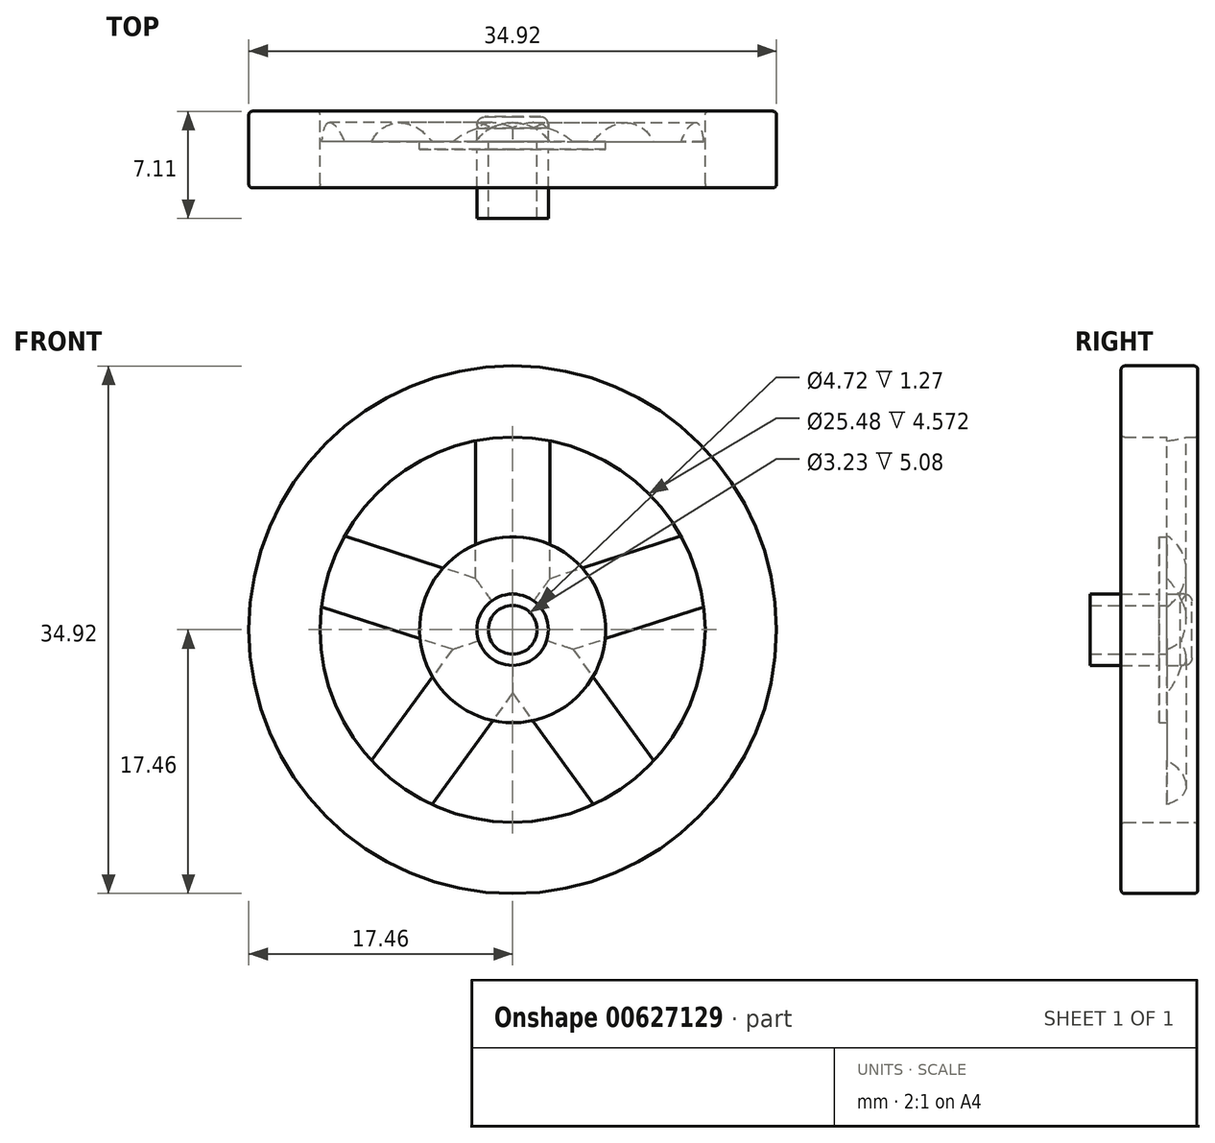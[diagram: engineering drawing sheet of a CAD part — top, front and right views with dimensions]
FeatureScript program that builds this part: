
annotation { "Feature Type Name" : "Feature", "Feature Type Description" : "" }
export const myFeature = defineFeature(function(context is Context, id is Id, definition is map)
    precondition{}
    {
        {
            var Q0;
            Q0=qCreatedBy(makeId("Front.planeOp"),FACE);
            var sketch = newSketch(context, id + "F0", { "sketchPlane" : qUnion([Q0])});
            skCircle(sketch, "E0", {"center": v(0, 0) * mm, "radius": 17.46 * mm});
            skCircle(sketch, "E1", {"center": v(0, 0) * mm, "radius": 6.16 * mm});
            skCircle(sketch, "E2", {"center": v(0, 0) * mm, "radius": 2.36 * mm});
            skLineSegment(sketch, "E3.trimOffspring", {"start": v(-2.46, 3.4) * mm, "end": v(-2.46, 12.5) * mm});
            skLineSegment(sketch, "E4.trimOffspring", {"start": v(2.46, 3.4) * mm, "end": v(2.46, 12.5) * mm});
            skCircle(sketch, "E5.0", {"center": v(0, 0) * mm, "radius": 12.74 * mm});
            skLineSegment(sketch, "E6.1.0", {"start": v(-3.99, -1.3) * mm, "end": v(-12.65, 1.52) * mm});
            skLineSegment(sketch, "E6.1.1", {"start": v(-2.46, 3.4) * mm, "end": v(-11.12, 6.2) * mm});
            skLineSegment(sketch, "E6.2.0", {"start": v(0, -4.2) * mm, "end": v(-5.35, -11.56) * mm});
            skLineSegment(sketch, "E6.2.1", {"start": v(-3.99, -1.3) * mm, "end": v(-9.34, -8.66) * mm});
            skLineSegment(sketch, "E6.3.0", {"start": v(3.99, -1.3) * mm, "end": v(9.34, -8.66) * mm});
            skLineSegment(sketch, "E6.3.1", {"start": v(0, -4.2) * mm, "end": v(5.35, -11.56) * mm});
            skLineSegment(sketch, "E6.4.0", {"start": v(2.46, 3.4) * mm, "end": v(11.12, 6.2) * mm});
            skLineSegment(sketch, "E6.4.1", {"start": v(3.99, -1.3) * mm, "end": v(12.65, 1.52) * mm});
            skSolve(sketch);
        }
        {
            var Q0;
            Q0=makeQuery(id+"F0.imprint","IMPRINT",FACE,{"disambiguationData":[TD([[makeQuery(id+"F0.imprint","IMPRINT",EDGE,{"derivedFrom":sQuery(id+"F0.wireOp",EDGE,"E2")}),-1.0]])]});
            var Q1;
            {var subQ0=sQuery(id+"F0.wireOp",EDGE,"E5.0");var subQ1=sQuery(id+"F0.wireOp",EDGE,"E3.trimOffspring");var subQ2=makeQuery(id+"F0.imprint","INTERSECT",VERTEX,{"derivedFrom":[subQ1,subQ0]});Q1=makeQuery(id+"F0.imprint","IMPRINT",FACE,{"disambiguationData":[TD([[makeQuery(id+"F0.imprint","IMPRINT",EDGE,{"disambiguationData":[TD([[subQ2,1.0]])],"derivedFrom":subQ1}),-1.0]])]});}
            var Q2;
            {var subQ0=sQuery(id+"F0.wireOp",EDGE,"E6.3.0");var subQ1=sQuery(id+"F0.wireOp",EDGE,"E5.0");var subQ2=makeQuery(id+"F0.imprint","INTERSECT",VERTEX,{"derivedFrom":[subQ1,subQ0]});Q2=makeQuery(id+"F0.imprint","IMPRINT",FACE,{"disambiguationData":[TD([[makeQuery(id+"F0.imprint","IMPRINT",EDGE,{"disambiguationData":[TD([[subQ2,1.0]])],"derivedFrom":subQ1}),1.0]])]});}
            var Q3;
            {var subQ0=sQuery(id+"F0.wireOp",EDGE,"E6.2.0");var subQ1=sQuery(id+"F0.wireOp",EDGE,"E5.0");var subQ2=makeQuery(id+"F0.imprint","INTERSECT",VERTEX,{"derivedFrom":[subQ1,subQ0]});Q3=makeQuery(id+"F0.imprint","IMPRINT",FACE,{"disambiguationData":[TD([[makeQuery(id+"F0.imprint","IMPRINT",EDGE,{"disambiguationData":[TD([[subQ2,1.0]])],"derivedFrom":subQ1}),1.0]])]});}
            var Q4;
            {var subQ0=sQuery(id+"F0.wireOp",EDGE,"E6.1.0");var subQ1=sQuery(id+"F0.wireOp",EDGE,"E5.0");var subQ2=makeQuery(id+"F0.imprint","INTERSECT",VERTEX,{"derivedFrom":[subQ1,subQ0]});Q4=makeQuery(id+"F0.imprint","IMPRINT",FACE,{"disambiguationData":[TD([[makeQuery(id+"F0.imprint","IMPRINT",EDGE,{"disambiguationData":[TD([[subQ2,1.0]])],"derivedFrom":subQ1}),1.0]])]});}
            var Q5;
            {var subQ0=sQuery(id+"F0.wireOp",EDGE,"E6.4.0");var subQ1=sQuery(id+"F0.wireOp",EDGE,"E5.0");var subQ2=makeQuery(id+"F0.imprint","INTERSECT",VERTEX,{"derivedFrom":[subQ1,subQ0]});Q5=makeQuery(id+"F0.imprint","IMPRINT",FACE,{"disambiguationData":[TD([[makeQuery(id+"F0.imprint","IMPRINT",EDGE,{"disambiguationData":[TD([[subQ2,1.0]])],"derivedFrom":subQ1}),1.0]])]});}
            extrude(context, id + "F1", {"entities" : qUnion([Q0, Q1, Q2, Q3, Q4, Q5]), "depth" : 1.27 * mm, "offsetDistance" : 25.4 * mm});
        }
        {
            var Q0;
            Q0=makeQuery(id+"F1.opExtrude","CAP_EDGE",EDGE,{"disambiguationData":[OSD([sQuery(id+"F0.wireOp",EDGE,"E6.2.0")])],"isStart":true});
            var Q1;
            Q1=makeQuery(id+"F1.opExtrude","CAP_EDGE",EDGE,{"disambiguationData":[OSD([sQuery(id+"F0.wireOp",EDGE,"E6.2.1")])],"isStart":true});
            var Q2;
            Q2=makeQuery(id+"F1.opExtrude","CAP_EDGE",EDGE,{"disambiguationData":[OSD([sQuery(id+"F0.wireOp",EDGE,"E6.1.0")])],"isStart":true});
            var Q3;
            Q3=makeQuery(id+"F1.opExtrude","CAP_EDGE",EDGE,{"disambiguationData":[OSD([sQuery(id+"F0.wireOp",EDGE,"E6.1.1")])],"isStart":true});
            var Q4;
            Q4=makeQuery(id+"F1.opExtrude","CAP_EDGE",EDGE,{"disambiguationData":[OSD([sQuery(id+"F0.wireOp",EDGE,"E4.trimOffspring")])],"isStart":true});
            var Q5;
            Q5=makeQuery(id+"F1.opExtrude","CAP_EDGE",EDGE,{"disambiguationData":[OSD([sQuery(id+"F0.wireOp",EDGE,"E3.trimOffspring")])],"isStart":true});
            var Q6;
            Q6=makeQuery(id+"F1.opExtrude","CAP_EDGE",EDGE,{"disambiguationData":[OSD([sQuery(id+"F0.wireOp",EDGE,"E6.4.1")])],"isStart":true});
            var Q7;
            Q7=makeQuery(id+"F1.opExtrude","CAP_EDGE",EDGE,{"disambiguationData":[OSD([sQuery(id+"F0.wireOp",EDGE,"E6.4.0")])],"isStart":true});
            var Q8;
            Q8=makeQuery(id+"F1.opExtrude","CAP_EDGE",EDGE,{"disambiguationData":[OSD([sQuery(id+"F0.wireOp",EDGE,"E6.3.0")])],"isStart":true});
            var Q9;
            Q9=makeQuery(id+"F1.opExtrude","CAP_EDGE",EDGE,{"disambiguationData":[OSD([sQuery(id+"F0.wireOp",EDGE,"E6.3.1")])],"isStart":true});
            fillet(context, id + "F2", {"entities" : qUnion([Q0, Q1, Q2, Q3, Q4, Q5, Q6, Q7, Q8, Q9]), "radius" : 3.02 * mm, "tangentPropagation" : true, "allowEdgeOverflow" : false});
        }
        {
            var Q0;
            Q0=makeQuery(id+"F0.imprint","IMPRINT",FACE,{"disambiguationData":[TD([[makeQuery(id+"F0.imprint","IMPRINT",EDGE,{"derivedFrom":sQuery(id+"F0.wireOp",EDGE,"E0")}),1.0]])]});
            extrude(context, id + "F3", {"entities" : qUnion([Q0]), "operationType" : NewBodyOperationType.ADD, "depth" : 4.32 * mm, "offsetDistance" : 25.4 * mm});
        }
        {
            var Q0;
            Q0=makeQuery(id+"F0.imprint","IMPRINT",FACE,{"disambiguationData":[TD([[makeQuery(id+"F0.imprint","IMPRINT",EDGE,{"derivedFrom":sQuery(id+"F0.wireOp",EDGE,"E2")}),1.0]])]});
            extrude(context, id + "F4", {"entities" : qUnion([Q0]), "endBound" : BoundingType.SYMMETRIC, "oppositeDirection" : true, "depth" : 0.76 * mm, "offsetDistance" : 25.4 * mm});
        }
        {
            var Q0;
            Q0=makeQuery(id+"F0.imprint","IMPRINT",FACE,{"disambiguationData":[TD([[makeQuery(id+"F0.imprint","IMPRINT",EDGE,{"derivedFrom":sQuery(id+"F0.wireOp",EDGE,"E0")}),1.0]])]});
            extrude(context, id + "F5", {"entities" : qUnion([Q0]), "operationType" : NewBodyOperationType.ADD, "oppositeDirection" : true, "depth" : 0.76 * mm, "offsetDistance" : 25.4 * mm});
        }
        {
            var Q0;
            Q0=makeQuery(id+"F4.opExtrude","CAP_EDGE",EDGE,{"disambiguationData":[OSD([sQuery(id+"F0.wireOp",EDGE,"E2")])],"isStart":false});
            fillet(context, id + "F6", {"entities" : qUnion([Q0]), "radius" : 0.5 * mm, "tangentPropagation" : true, "allowEdgeOverflow" : false});
        }
        {
            var Q0;
            Q0=makeQuery(id+"F1.opExtrude","CAP_FACE",FACE,{"disambiguationData":[OSD([sQuery(id+"F0.wireOp",EDGE,"E2"),sQuery(id+"F0.wireOp",EDGE,"E3.trimOffspring"),sQuery(id+"F0.wireOp",EDGE,"E4.trimOffspring"),sQuery(id+"F0.wireOp",EDGE,"E5.0"),sQuery(id+"F0.wireOp",EDGE,"E6.1.0"),sQuery(id+"F0.wireOp",EDGE,"E6.1.1"),sQuery(id+"F0.wireOp",EDGE,"E6.2.0"),sQuery(id+"F0.wireOp",EDGE,"E6.2.1"),sQuery(id+"F0.wireOp",EDGE,"E6.3.0"),sQuery(id+"F0.wireOp",EDGE,"E6.3.1"),sQuery(id+"F0.wireOp",EDGE,"E6.4.0"),sQuery(id+"F0.wireOp",EDGE,"E6.4.1")])],"isStart":false});
            var sketch = newSketch(context, id + "F7", { "sketchPlane" : qUnion([Q0])});
            skCircle(sketch, "E7", {"center": v(0, 0) * mm, "radius": 6.16 * mm});
            skCircle(sketch, "E8", {"center": v(0, 0) * mm, "radius": 1.61 * mm});
            skSolve(sketch);
        }
        {
            var Q0;
            {var subQ10=sQuery(id+"F0.wireOp",EDGE,"E2");Q0=makeQuery(id+"F7.imprint","IMPRINT",FACE,{"disambiguationData":[TD([[makeQuery(id+"F7.imprint","IMPRINT",EDGE,{"derivedFrom":makeQuery(id+"F1.opExtrude","CAP_EDGE",EDGE,{"disambiguationData":[OSD([subQ10])],"isStart":false})}),-1.0]])]});}
            var Q1;
            {var subQ0=sQuery(id+"F7.wireOp",EDGE,"E7");var subQ1=sQuery(id+"F0.wireOp",EDGE,"E6.1.1");var subQ2=sQuery(id+"F0.wireOp",EDGE,"E3.trimOffspring");var subQ3=makeQuery(id+"F1.opExtrude","CAP_FACE",FACE,{"disambiguationData":[OSD([sQuery(id+"F0.wireOp",EDGE,"E2"),subQ2,sQuery(id+"F0.wireOp",EDGE,"E4.trimOffspring"),sQuery(id+"F0.wireOp",EDGE,"E5.0"),sQuery(id+"F0.wireOp",EDGE,"E6.1.0"),subQ1,sQuery(id+"F0.wireOp",EDGE,"E6.2.0"),sQuery(id+"F0.wireOp",EDGE,"E6.2.1"),sQuery(id+"F0.wireOp",EDGE,"E6.3.0"),sQuery(id+"F0.wireOp",EDGE,"E6.3.1"),sQuery(id+"F0.wireOp",EDGE,"E6.4.0"),sQuery(id+"F0.wireOp",EDGE,"E6.4.1")])],"isStart":false});var subQ4=makeQuery(id+"F2.opFillet","BLEND_EDGE",EDGE,{"blendedFrom":[makeQuery(id+"F1.opExtrude","CAP_EDGE",EDGE,{"disambiguationData":[OSD([subQ2])],"isStart":true}),subQ3],"blendedInto":[subQ3]});var subQ5=makeQuery(id+"F7.imprint","INTERSECT",VERTEX,{"derivedFrom":[subQ4,subQ0]});Q1=makeQuery(id+"F7.imprint","IMPRINT",FACE,{"disambiguationData":[TD([[makeQuery(id+"F7.imprint","IMPRINT",EDGE,{"disambiguationData":[TD([[subQ5,-1.0]])],"derivedFrom":subQ0}),1.0]])]});}
            var Q2;
            {var subQ0=sQuery(id+"F7.wireOp",EDGE,"E7");var subQ1=sQuery(id+"F0.wireOp",EDGE,"E6.4.0");var subQ2=sQuery(id+"F0.wireOp",EDGE,"E4.trimOffspring");var subQ3=makeQuery(id+"F1.opExtrude","CAP_FACE",FACE,{"disambiguationData":[OSD([sQuery(id+"F0.wireOp",EDGE,"E2"),sQuery(id+"F0.wireOp",EDGE,"E3.trimOffspring"),subQ2,sQuery(id+"F0.wireOp",EDGE,"E5.0"),sQuery(id+"F0.wireOp",EDGE,"E6.1.0"),sQuery(id+"F0.wireOp",EDGE,"E6.1.1"),sQuery(id+"F0.wireOp",EDGE,"E6.2.0"),sQuery(id+"F0.wireOp",EDGE,"E6.2.1"),sQuery(id+"F0.wireOp",EDGE,"E6.3.0"),sQuery(id+"F0.wireOp",EDGE,"E6.3.1"),subQ1,sQuery(id+"F0.wireOp",EDGE,"E6.4.1")])],"isStart":false});var subQ4=makeQuery(id+"F2.opFillet","BLEND_EDGE",EDGE,{"blendedFrom":[makeQuery(id+"F1.opExtrude","CAP_EDGE",EDGE,{"disambiguationData":[OSD([subQ2])],"isStart":true}),subQ3],"blendedInto":[subQ3]});var subQ5=makeQuery(id+"F7.imprint","INTERSECT",VERTEX,{"derivedFrom":[subQ4,subQ0]});Q2=makeQuery(id+"F7.imprint","IMPRINT",FACE,{"disambiguationData":[TD([[makeQuery(id+"F7.imprint","IMPRINT",EDGE,{"disambiguationData":[TD([[subQ5,1.0]])],"derivedFrom":subQ0}),1.0]])]});}
            var Q3;
            {var subQ0=sQuery(id+"F7.wireOp",EDGE,"E7");var subQ1=sQuery(id+"F0.wireOp",EDGE,"E6.2.1");var subQ2=sQuery(id+"F0.wireOp",EDGE,"E6.1.0");var subQ3=makeQuery(id+"F1.opExtrude","CAP_FACE",FACE,{"disambiguationData":[OSD([sQuery(id+"F0.wireOp",EDGE,"E2"),sQuery(id+"F0.wireOp",EDGE,"E3.trimOffspring"),sQuery(id+"F0.wireOp",EDGE,"E4.trimOffspring"),sQuery(id+"F0.wireOp",EDGE,"E5.0"),subQ2,sQuery(id+"F0.wireOp",EDGE,"E6.1.1"),sQuery(id+"F0.wireOp",EDGE,"E6.2.0"),subQ1,sQuery(id+"F0.wireOp",EDGE,"E6.3.0"),sQuery(id+"F0.wireOp",EDGE,"E6.3.1"),sQuery(id+"F0.wireOp",EDGE,"E6.4.0"),sQuery(id+"F0.wireOp",EDGE,"E6.4.1")])],"isStart":false});var subQ4=makeQuery(id+"F2.opFillet","BLEND_EDGE",EDGE,{"blendedFrom":[makeQuery(id+"F1.opExtrude","CAP_EDGE",EDGE,{"disambiguationData":[OSD([subQ2])],"isStart":true}),subQ3],"blendedInto":[subQ3]});var subQ5=makeQuery(id+"F7.imprint","INTERSECT",VERTEX,{"derivedFrom":[subQ4,subQ0]});Q3=makeQuery(id+"F7.imprint","IMPRINT",FACE,{"disambiguationData":[TD([[makeQuery(id+"F7.imprint","IMPRINT",EDGE,{"disambiguationData":[TD([[subQ5,-1.0]])],"derivedFrom":subQ0}),1.0]])]});}
            var Q4;
            {var subQ0=sQuery(id+"F7.wireOp",EDGE,"E7");var subQ1=sQuery(id+"F0.wireOp",EDGE,"E6.3.1");var subQ2=sQuery(id+"F0.wireOp",EDGE,"E6.2.0");var subQ3=makeQuery(id+"F1.opExtrude","CAP_FACE",FACE,{"disambiguationData":[OSD([sQuery(id+"F0.wireOp",EDGE,"E2"),sQuery(id+"F0.wireOp",EDGE,"E3.trimOffspring"),sQuery(id+"F0.wireOp",EDGE,"E4.trimOffspring"),sQuery(id+"F0.wireOp",EDGE,"E5.0"),sQuery(id+"F0.wireOp",EDGE,"E6.1.0"),sQuery(id+"F0.wireOp",EDGE,"E6.1.1"),subQ2,sQuery(id+"F0.wireOp",EDGE,"E6.2.1"),sQuery(id+"F0.wireOp",EDGE,"E6.3.0"),subQ1,sQuery(id+"F0.wireOp",EDGE,"E6.4.0"),sQuery(id+"F0.wireOp",EDGE,"E6.4.1")])],"isStart":false});var subQ4=makeQuery(id+"F2.opFillet","BLEND_EDGE",EDGE,{"blendedFrom":[makeQuery(id+"F1.opExtrude","CAP_EDGE",EDGE,{"disambiguationData":[OSD([subQ2])],"isStart":true}),subQ3],"blendedInto":[subQ3]});var subQ5=makeQuery(id+"F7.imprint","INTERSECT",VERTEX,{"derivedFrom":[subQ4,subQ0]});Q4=makeQuery(id+"F7.imprint","IMPRINT",FACE,{"disambiguationData":[TD([[makeQuery(id+"F7.imprint","IMPRINT",EDGE,{"disambiguationData":[TD([[subQ5,-1.0]])],"derivedFrom":subQ0}),1.0]])]});}
            var Q5;
            {var subQ0=sQuery(id+"F7.wireOp",EDGE,"E7");var subQ1=sQuery(id+"F0.wireOp",EDGE,"E6.4.1");var subQ2=sQuery(id+"F0.wireOp",EDGE,"E6.3.0");var subQ3=makeQuery(id+"F1.opExtrude","CAP_FACE",FACE,{"disambiguationData":[OSD([sQuery(id+"F0.wireOp",EDGE,"E2"),sQuery(id+"F0.wireOp",EDGE,"E3.trimOffspring"),sQuery(id+"F0.wireOp",EDGE,"E4.trimOffspring"),sQuery(id+"F0.wireOp",EDGE,"E5.0"),sQuery(id+"F0.wireOp",EDGE,"E6.1.0"),sQuery(id+"F0.wireOp",EDGE,"E6.1.1"),sQuery(id+"F0.wireOp",EDGE,"E6.2.0"),sQuery(id+"F0.wireOp",EDGE,"E6.2.1"),subQ2,sQuery(id+"F0.wireOp",EDGE,"E6.3.1"),sQuery(id+"F0.wireOp",EDGE,"E6.4.0"),subQ1])],"isStart":false});var subQ4=makeQuery(id+"F2.opFillet","BLEND_EDGE",EDGE,{"blendedFrom":[makeQuery(id+"F1.opExtrude","CAP_EDGE",EDGE,{"disambiguationData":[OSD([subQ2])],"isStart":true}),subQ3],"blendedInto":[subQ3]});var subQ5=makeQuery(id+"F7.imprint","INTERSECT",VERTEX,{"derivedFrom":[subQ4,subQ0]});Q5=makeQuery(id+"F7.imprint","IMPRINT",FACE,{"disambiguationData":[TD([[makeQuery(id+"F7.imprint","IMPRINT",EDGE,{"disambiguationData":[TD([[subQ5,-1.0]])],"derivedFrom":subQ0}),1.0]])]});}
            extrude(context, id + "F8", {"entities" : qUnion([Q0, Q1, Q2, Q3, Q4, Q5]), "operationType" : NewBodyOperationType.ADD, "depth" : 0.5 * mm, "offsetDistance" : 25.4 * mm});
        }
        {
            var Q0;
            Q0=makeQuery(id+"F7.imprint","IMPRINT",FACE,{"disambiguationData":[TD([[makeQuery(id+"F7.imprint","IMPRINT",EDGE,{"derivedFrom":sQuery(id+"F7.wireOp",EDGE,"E8")}),-1.0]])]});
            extrude(context, id + "F9", {"entities" : qUnion([Q0]), "operationType" : NewBodyOperationType.ADD, "depth" : 5.08 * mm, "offsetDistance" : 25.4 * mm});
        }
        {
            var Q0;
            Q0=makeQuery(id+"F5.opExtrude","CAP_EDGE",EDGE,{"disambiguationData":[OSD([sQuery(id+"F0.wireOp",EDGE,"E0")])],"isStart":false});
            var Q1;
            Q1=makeQuery(id+"F3.opExtrude","CAP_EDGE",EDGE,{"disambiguationData":[OSD([sQuery(id+"F0.wireOp",EDGE,"E0")])],"isStart":false});
            var Q2;
            Q2=makeQuery(id+"F5.opExtrude","CAP_EDGE",EDGE,{"disambiguationData":[OSD([sQuery(id+"F0.wireOp",EDGE,"E5.0")])],"isStart":false});
            var Q3;
            Q3=makeQuery(id+"F3.opExtrude","CAP_EDGE",EDGE,{"disambiguationData":[OSD([sQuery(id+"F0.wireOp",EDGE,"E5.0")])],"isStart":false});
            fillet(context, id + "F10", {"entities" : qUnion([Q0, Q1, Q2, Q3]), "radius" : 0.25 * mm, "tangentPropagation" : true, "allowEdgeOverflow" : false});
        }
    });
